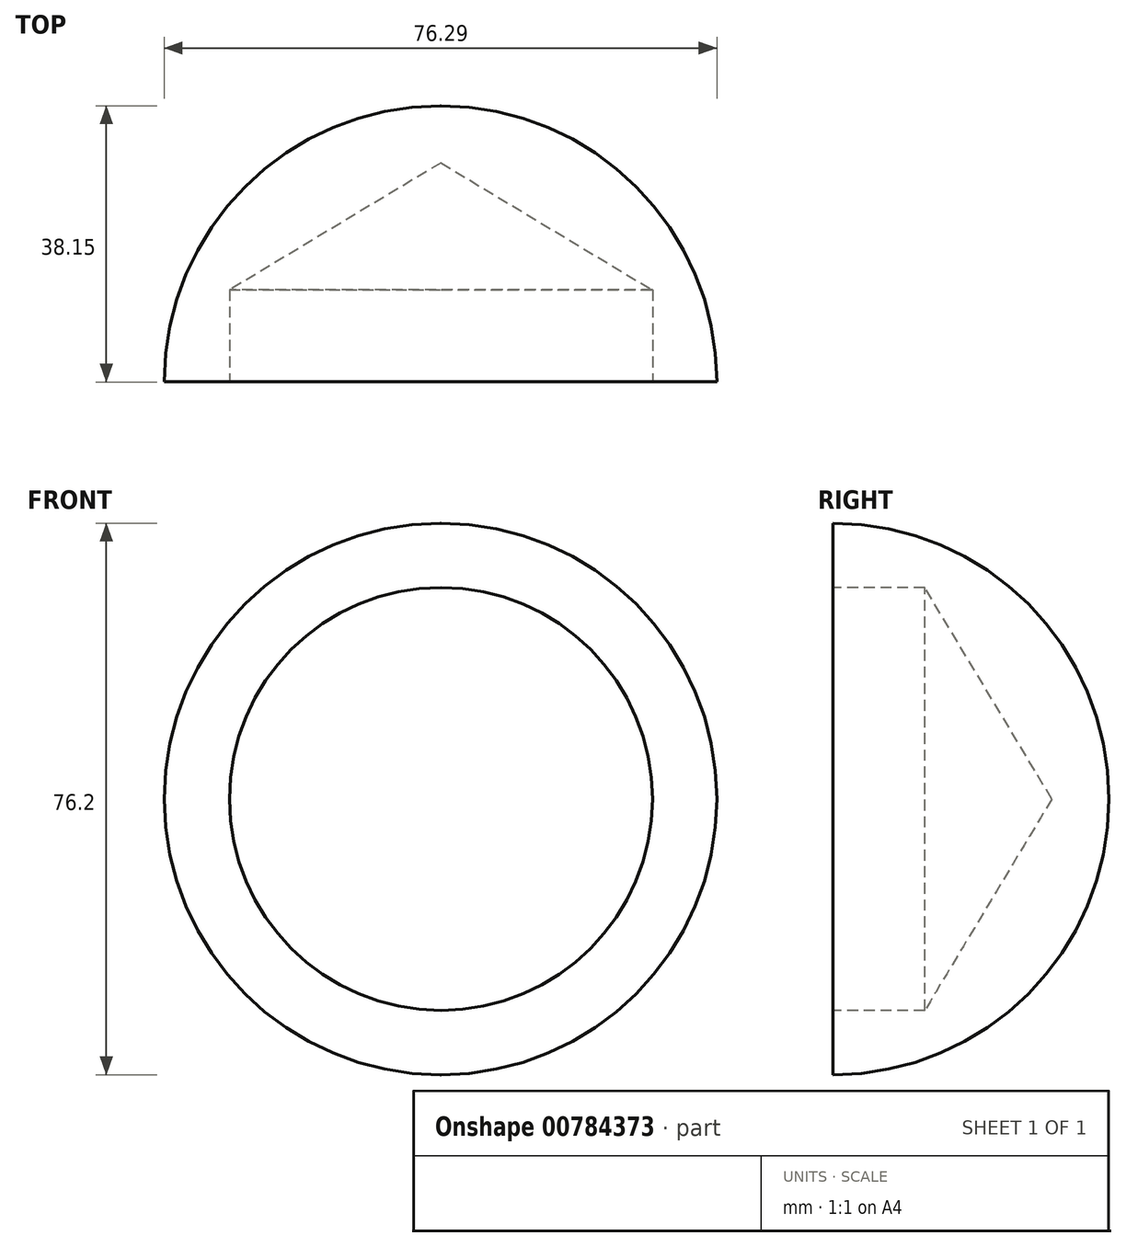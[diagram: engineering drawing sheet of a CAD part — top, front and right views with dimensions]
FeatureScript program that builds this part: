
annotation { "Feature Type Name" : "Feature", "Feature Type Description" : "" }
export const myFeature = defineFeature(function(context is Context, id is Id, definition is map)
    precondition{}
    {
        {
            var Q0;
            Q0=qCreatedBy(makeId("Top.planeOp"),FACE);
            var sketch = newSketch(context, id + "F0", { "sketchPlane" : qUnion([Q0])});
            skLineSegment(sketch, "E0.bottom", {"start": v(-40.12, 33.38) * mm, "end": v(36.17, 33.38) * mm});
            skLineSegment(sketch, "E0.top", {"start": v(-40.12, -4.77) * mm, "end": v(36.17, -4.77) * mm});
            skLineSegment(sketch, "E0.left", {"start": v(-40.12, 33.38) * mm, "end": v(-40.12, -4.77) * mm});
            skLineSegment(sketch, "E0.right", {"start": v(36.17, 33.38) * mm, "end": v(36.17, -4.77) * mm});
            skSolve(sketch);
        }
        {
            var Q0;
            Q0=makeQuery(id+"F0.imprint","IMPRINT",FACE,{"disambiguationData":[TD([[makeQuery(id+"F0.imprint","IMPRINT",EDGE,{"derivedFrom":sQuery(id+"F0.wireOp",EDGE,"E0.bottom")}),-1.0]])]});
            extrude(context, id + "F1", {"entities" : qUnion([Q0]), "depth" : 76.2 * mm, "offsetDistance" : 25.4 * mm});
        }
        {
            var Q0;
            Q0=makeQuery(id+"F1.opExtrude","CAP_EDGE",EDGE,{"disambiguationData":[OSD([sQuery(id+"F0.wireOp",EDGE,"E0.left")])],"isStart":false});
            var Q1;
            Q1=makeQuery(id+"F1.opExtrude","CAP_EDGE",EDGE,{"disambiguationData":[OSD([sQuery(id+"F0.wireOp",EDGE,"E0.left")])],"isStart":true});
            var Q2;
            Q2=makeQuery(id+"F1.opExtrude","CAP_EDGE",EDGE,{"disambiguationData":[OSD([sQuery(id+"F0.wireOp",EDGE,"E0.right")])],"isStart":true});
            var Q3;
            Q3=makeQuery(id+"F1.opExtrude","CAP_EDGE",EDGE,{"disambiguationData":[OSD([sQuery(id+"F0.wireOp",EDGE,"E0.right")])],"isStart":false});
            fillet(context, id + "F2", {"entities" : qUnion([Q0, Q1, Q2, Q3]), "radius" : 38.1 * mm, "tangentPropagation" : true, "allowEdgeOverflow" : false});
        }
        {
            var Q0;
            Q0=makeQuery(id+"F1.opExtrude","SWEPT_FACE",FACE,{"disambiguationData":[OSD([sQuery(id+"F0.wireOp",EDGE,"E0.top")])]});
            var sketch = newSketch(context, id + "F3", { "sketchPlane" : qUnion([Q0])});
            skCircle(sketch, "E1", {"center": v(-1.93, 38.1) * mm, "radius": 29.3 * mm});
            skSolve(sketch);
        }
        {
            var Q0;
            Q0=makeQuery(id+"F2.opFillet","BLEND_EDGE",EDGE,{"blendedFrom":[makeQuery(id+"F1.opExtrude","CAP_EDGE",EDGE,{"disambiguationData":[OSD([sQuery(id+"F0.wireOp",EDGE,"E0.left")])],"isStart":true}),makeQuery(id+"F1.opExtrude","SWEPT_FACE",FACE,{"disambiguationData":[OSD([sQuery(id+"F0.wireOp",EDGE,"E0.bottom")])]})],"blendedInto":[makeQuery(id+"F1.opExtrude","SWEPT_FACE",FACE,{"disambiguationData":[OSD([sQuery(id+"F0.wireOp",EDGE,"E0.bottom")])]})]});
            var Q1;
            Q1=makeQuery(id+"F2.opFillet","BLEND_EDGE",EDGE,{"blendedFrom":[makeQuery(id+"F1.opExtrude","CAP_EDGE",EDGE,{"disambiguationData":[OSD([sQuery(id+"F0.wireOp",EDGE,"E0.right")])],"isStart":true}),makeQuery(id+"F1.opExtrude","SWEPT_FACE",FACE,{"disambiguationData":[OSD([sQuery(id+"F0.wireOp",EDGE,"E0.bottom")])]})],"blendedInto":[makeQuery(id+"F1.opExtrude","SWEPT_FACE",FACE,{"disambiguationData":[OSD([sQuery(id+"F0.wireOp",EDGE,"E0.bottom")])]})]});
            fillet(context, id + "F4", {"entities" : qUnion([Q0, Q1]), "radius" : 38.1 * mm, "tangentPropagation" : true, "allowEdgeOverflow" : false});
        }
        {
            var Q0;
            Q0=sQuery(id+"F3.wireOp",VERTEX,"E1.center");
            var Q1;
            Q1=makeQuery(id+"F1.opExtrude","SWEPT_BODY",BODY,{"disambiguationData":[OSD([sQuery(id+"F0.wireOp",EDGE,"E0.bottom"),sQuery(id+"F0.wireOp",EDGE,"E0.top"),sQuery(id+"F0.wireOp",EDGE,"E0.left"),sQuery(id+"F0.wireOp",EDGE,"E0.right")])]});
            hole(context, id + "F5", {"style" : HoleStyle.SIMPLE, "endStyle" : HoleEndStyle.BLIND, "holeDiameter" : 58.42 * mm, "majorDiameter" : 6.35 * mm, "holeDepth" : 12.7 * mm, "isTappedThrough" : true, "tappedDepth" : 12.7 * mm, "tapClearance" : 3, "locations" : qUnion([Q0]), "scope" : qUnion([Q1])});
        }
    });
